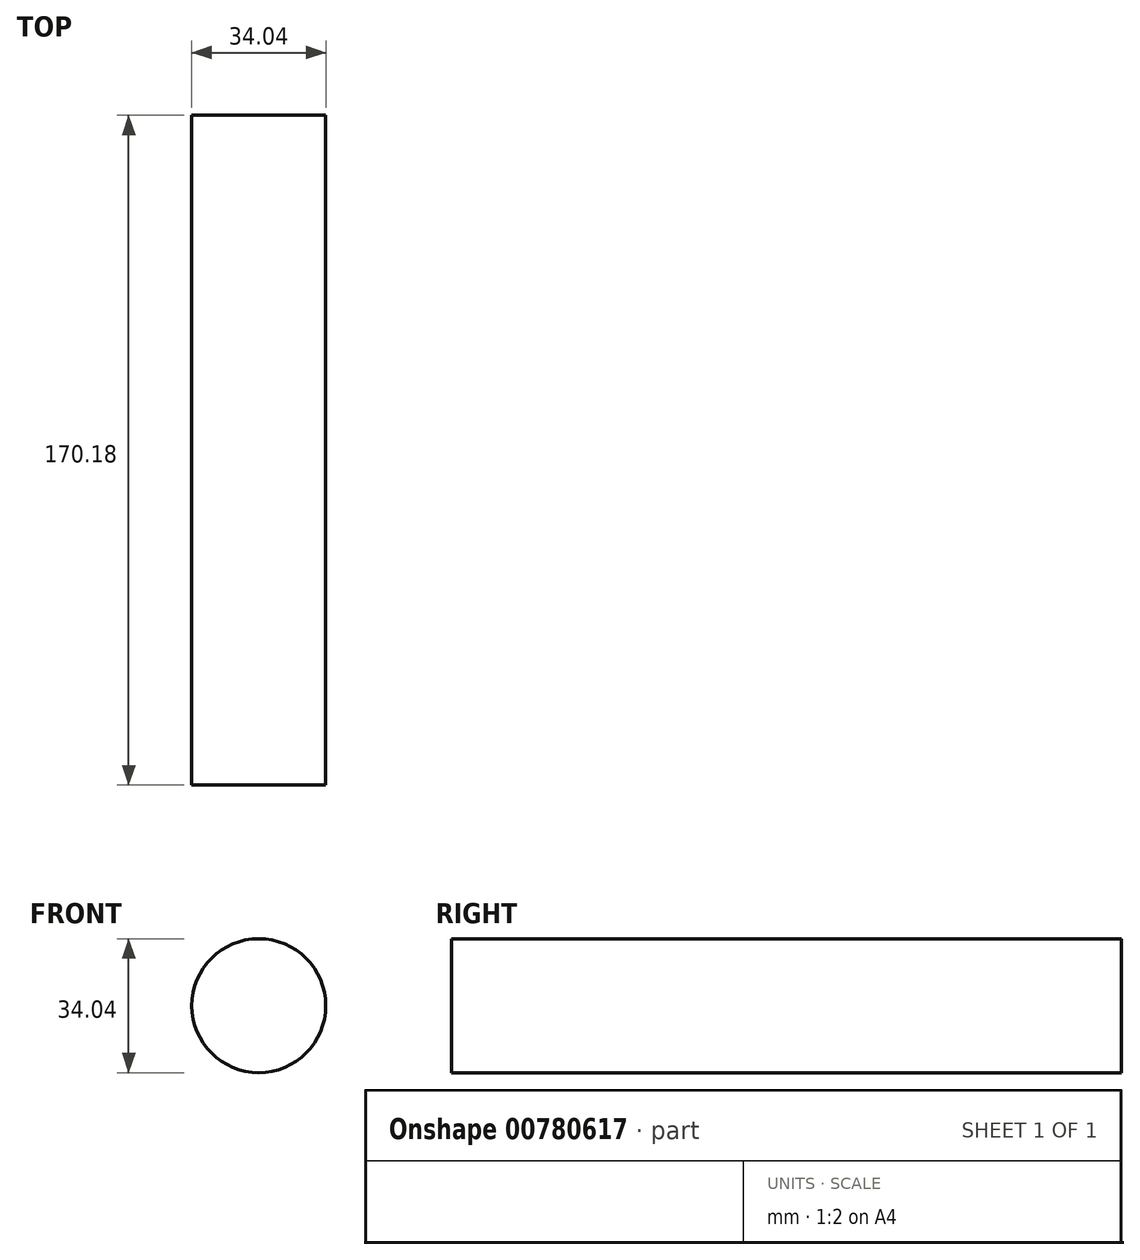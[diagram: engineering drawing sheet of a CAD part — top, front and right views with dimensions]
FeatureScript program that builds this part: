
annotation { "Feature Type Name" : "Feature", "Feature Type Description" : "" }
export const myFeature = defineFeature(function(context is Context, id is Id, definition is map)
    precondition{}
    {
        {
            var Q0;
            Q0=qCreatedBy(makeId("Front.planeOp"),FACE);
            var sketch = newSketch(context, id + "F0", { "sketchPlane" : qUnion([Q0])});
            skCircle(sketch, "E0", {"center": v(0, 0) * mm, "radius": 17.02 * mm});
            skSolve(sketch);
        }
        {
            var Q0;
            Q0 = qSketchRegion(id + "F0", true);
            extrude(context, id + "F1", {"entities" : qUnion([Q0]), "depth" : 170.18 * mm, "offsetDistance" : 25.4 * mm});
        }
    });
